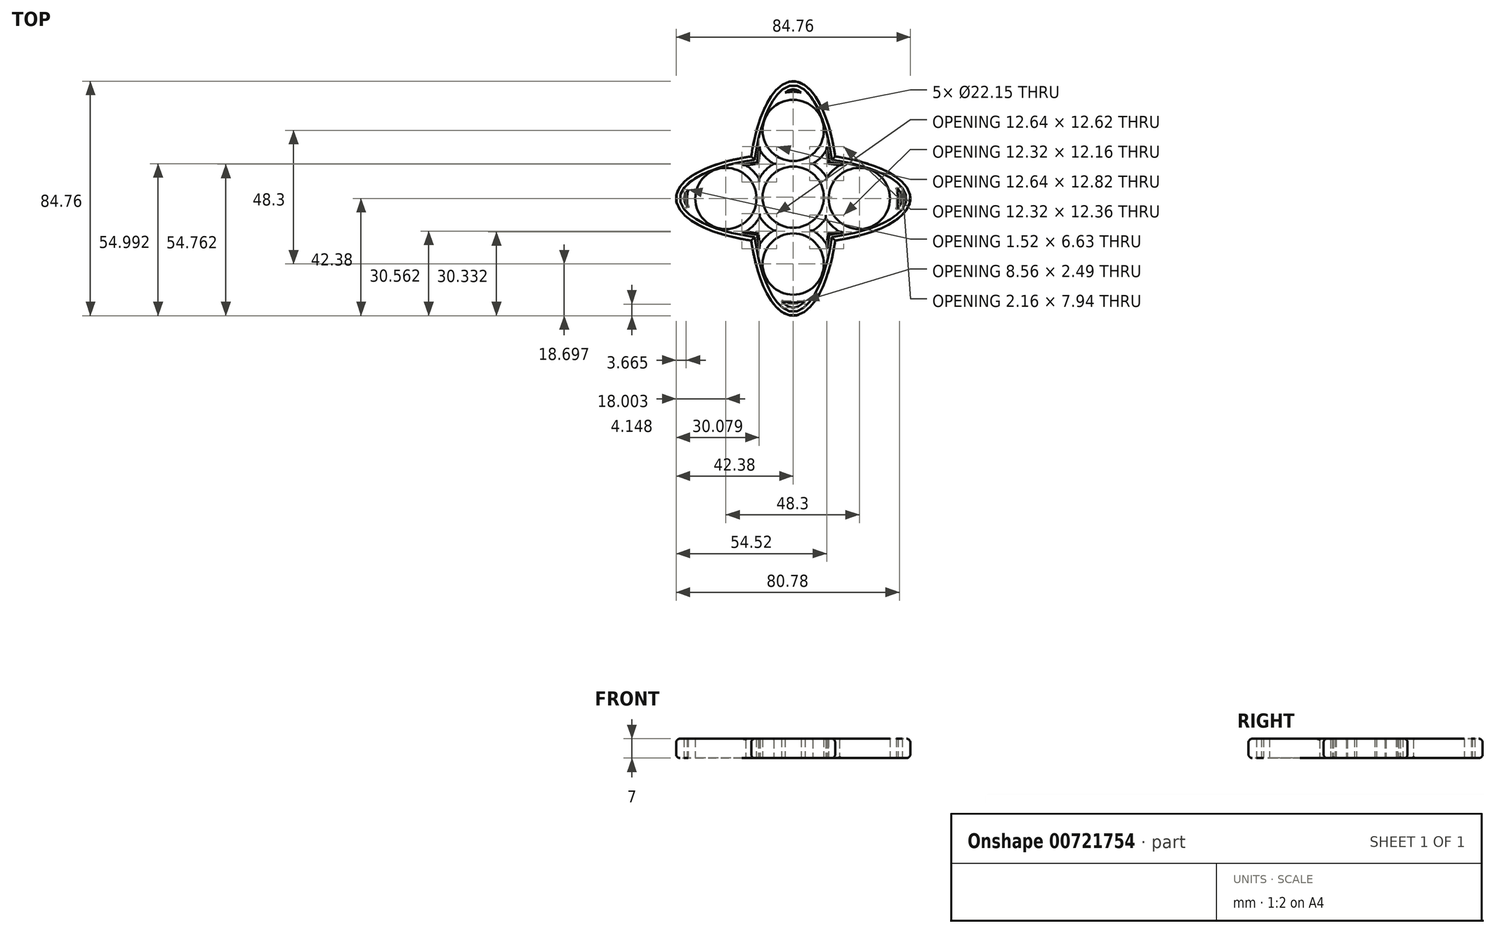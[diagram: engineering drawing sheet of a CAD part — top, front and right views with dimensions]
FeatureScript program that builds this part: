
annotation { "Feature Type Name" : "Feature", "Feature Type Description" : "" }
export const myFeature = defineFeature(function(context is Context, id is Id, definition is map)
    precondition{}
    {
        {
            var Q0;
            Q0=qCreatedBy(makeId("Top.planeOp"),FACE);
            var sketch = newSketch(context, id + "F0", { "sketchPlane" : qUnion([Q0])});
            skCircle(sketch, "E0", {"center": v(0, 0.47) * mm, "radius": 11.07 * mm});
            skCircle(sketch, "E1", {"center": v(0, -23.68) * mm, "radius": 11.07 * mm});
            skCircle(sketch, "E2", {"center": v(0, 24.62) * mm, "radius": 11.07 * mm});
            skCircle(sketch, "E3", {"center": v(23.92, 0) * mm, "radius": 11.07 * mm});
            skCircle(sketch, "E4", {"center": v(-24.38, 0) * mm, "radius": 11.07 * mm});
            skEllipse(sketch, "E5", {"center": v(0, 0) * mm, "majorRadius": 42.38 * mm, "minorRadius": 16.28 * mm, "majorAxis": v(0, -1)});
            skEllipse(sketch, "E6", {"center": v(0, 0) * mm, "majorRadius": 42.38 * mm, "minorRadius": 16.28 * mm, "majorAxis": v(1, 0)});
            skSolve(sketch);
        }
        {
            var Q0;
            {var subQ0=sQuery(id+"F0.wireOp",EDGE,"E6");var subQ1=sQuery(id+"F0.wireOp",EDGE,"E2");var subQ2=makeQuery(id+"F0.imprint","INTERSECT",VERTEX,{"disambiguationData":[OD(0.0)],"derivedFrom":[subQ1,subQ0]});Q0=makeQuery(id+"F0.imprint","IMPRINT",FACE,{"disambiguationData":[TD([[makeQuery(id+"F0.imprint","IMPRINT",EDGE,{"disambiguationData":[TD([[subQ2,-1.0]])],"derivedFrom":subQ1}),-1.0]])]});}
            var Q1;
            Q1=makeQuery(id+"F0.imprint","IMPRINT",FACE,{"disambiguationData":[TD([[makeQuery(id+"F0.imprint","IMPRINT",EDGE,{"derivedFrom":sQuery(id+"F0.wireOp",EDGE,"E0")}),-1.0]])]});
            var Q2;
            {var subQ0=sQuery(id+"F0.wireOp",EDGE,"E5");var subQ1=sQuery(id+"F0.wireOp",EDGE,"E4");var subQ2=makeQuery(id+"F0.imprint","INTERSECT",VERTEX,{"disambiguationData":[OD(0.0)],"derivedFrom":[subQ1,subQ0]});Q2=makeQuery(id+"F0.imprint","IMPRINT",FACE,{"disambiguationData":[TD([[makeQuery(id+"F0.imprint","IMPRINT",EDGE,{"disambiguationData":[TD([[subQ2,-1.0]])],"derivedFrom":subQ1}),-1.0]])]});}
            var Q3;
            {var subQ0=sQuery(id+"F0.wireOp",EDGE,"E6");var subQ1=sQuery(id+"F0.wireOp",EDGE,"E1");var subQ2=makeQuery(id+"F0.imprint","INTERSECT",VERTEX,{"disambiguationData":[OD(0.0)],"derivedFrom":[subQ1,subQ0]});Q3=makeQuery(id+"F0.imprint","IMPRINT",FACE,{"disambiguationData":[TD([[makeQuery(id+"F0.imprint","IMPRINT",EDGE,{"disambiguationData":[TD([[subQ2,-1.0]])],"derivedFrom":subQ1}),-1.0]])]});}
            var Q4;
            {var subQ0=sQuery(id+"F0.wireOp",EDGE,"E5");var subQ1=sQuery(id+"F0.wireOp",EDGE,"E3");var subQ2=makeQuery(id+"F0.imprint","INTERSECT",VERTEX,{"disambiguationData":[OD(0.0)],"derivedFrom":[subQ1,subQ0]});Q4=makeQuery(id+"F0.imprint","IMPRINT",FACE,{"disambiguationData":[TD([[makeQuery(id+"F0.imprint","IMPRINT",EDGE,{"disambiguationData":[TD([[subQ2,-1.0]])],"derivedFrom":subQ1}),-1.0]])]});}
            extrude(context, id + "F1", {"entities" : qUnion([Q0, Q1, Q2, Q3, Q4]), "depth" : 7 * mm, "offsetDistance" : 25 * mm});
        }
        {
            var Q0;
            {var subQ0=sQuery(id+"F0.wireOp",EDGE,"E6");var subQ1=sQuery(id+"F0.wireOp",EDGE,"E5");Q0=makeQuery(id+"F1.opExtrude","CAP_EDGE",EDGE,{"disambiguationData":[OSD([subQ1]),TDD([makeQuery(id+"F0.imprint","IMPRINT",EDGE,{"disambiguationData":[TD([[makeQuery(id+"F0.imprint","INTERSECT",VERTEX,{"disambiguationData":[OD(1.0)],"derivedFrom":[subQ1,subQ0]}),-1.0]])],"derivedFrom":subQ1})])],"isStart":false});}
            var Q1;
            {var subQ0=sQuery(id+"F0.wireOp",EDGE,"E6");var subQ1=sQuery(id+"F0.wireOp",EDGE,"E5");Q1=makeQuery(id+"F1.opExtrude","CAP_EDGE",EDGE,{"disambiguationData":[OSD([subQ0]),TDD([makeQuery(id+"F0.imprint","IMPRINT",EDGE,{"disambiguationData":[TD([[makeQuery(id+"F0.imprint","INTERSECT",VERTEX,{"disambiguationData":[OD(0.0)],"derivedFrom":[subQ1,subQ0]}),-1.0]])],"derivedFrom":subQ0})])],"isStart":false});}
            var Q2;
            {var subQ0=sQuery(id+"F0.wireOp",EDGE,"E6");var subQ1=sQuery(id+"F0.wireOp",EDGE,"E5");Q2=makeQuery(id+"F1.opExtrude","CAP_EDGE",EDGE,{"disambiguationData":[OSD([subQ1]),TDD([makeQuery(id+"F0.imprint","IMPRINT",EDGE,{"disambiguationData":[TD([[makeQuery(id+"F0.imprint","INTERSECT",VERTEX,{"disambiguationData":[OD(0.0)],"derivedFrom":[subQ1,subQ0]}),1.0]])],"derivedFrom":subQ1})])],"isStart":false});}
            var Q3;
            {var subQ0=sQuery(id+"F0.wireOp",EDGE,"E6");var subQ1=sQuery(id+"F0.wireOp",EDGE,"E5");Q3=makeQuery(id+"F1.opExtrude","CAP_EDGE",EDGE,{"disambiguationData":[OSD([subQ0]),TDD([makeQuery(id+"F0.imprint","IMPRINT",EDGE,{"disambiguationData":[TD([[makeQuery(id+"F0.imprint","INTERSECT",VERTEX,{"disambiguationData":[OD(2.0)],"derivedFrom":[subQ1,subQ0]}),-1.0]])],"derivedFrom":subQ0})])],"isStart":false});}
            var Q4;
            {var subQ0=sQuery(id+"F0.wireOp",EDGE,"E6");var subQ1=sQuery(id+"F0.wireOp",EDGE,"E5");Q4=makeQuery(id+"F1.opExtrude","CAP_EDGE",EDGE,{"disambiguationData":[OSD([subQ0]),TDD([makeQuery(id+"F0.imprint","IMPRINT",EDGE,{"disambiguationData":[TD([[makeQuery(id+"F0.imprint","INTERSECT",VERTEX,{"disambiguationData":[OD(0.0)],"derivedFrom":[subQ1,subQ0]}),-1.0]])],"derivedFrom":subQ0})])],"isStart":true});}
            var Q5;
            {var subQ0=sQuery(id+"F0.wireOp",EDGE,"E6");var subQ1=sQuery(id+"F0.wireOp",EDGE,"E5");Q5=makeQuery(id+"F1.opExtrude","CAP_EDGE",EDGE,{"disambiguationData":[OSD([subQ1]),TDD([makeQuery(id+"F0.imprint","IMPRINT",EDGE,{"disambiguationData":[TD([[makeQuery(id+"F0.imprint","INTERSECT",VERTEX,{"disambiguationData":[OD(0.0)],"derivedFrom":[subQ1,subQ0]}),1.0]])],"derivedFrom":subQ1})])],"isStart":true});}
            var Q6;
            {var subQ0=sQuery(id+"F0.wireOp",EDGE,"E6");var subQ1=sQuery(id+"F0.wireOp",EDGE,"E5");Q6=makeQuery(id+"F1.opExtrude","CAP_EDGE",EDGE,{"disambiguationData":[OSD([subQ0]),TDD([makeQuery(id+"F0.imprint","IMPRINT",EDGE,{"disambiguationData":[TD([[makeQuery(id+"F0.imprint","INTERSECT",VERTEX,{"disambiguationData":[OD(2.0)],"derivedFrom":[subQ1,subQ0]}),-1.0]])],"derivedFrom":subQ0})])],"isStart":true});}
            var Q7;
            {var subQ0=sQuery(id+"F0.wireOp",EDGE,"E6");var subQ1=sQuery(id+"F0.wireOp",EDGE,"E5");Q7=makeQuery(id+"F1.opExtrude","CAP_EDGE",EDGE,{"disambiguationData":[OSD([subQ1]),TDD([makeQuery(id+"F0.imprint","IMPRINT",EDGE,{"disambiguationData":[TD([[makeQuery(id+"F0.imprint","INTERSECT",VERTEX,{"disambiguationData":[OD(1.0)],"derivedFrom":[subQ1,subQ0]}),-1.0]])],"derivedFrom":subQ1})])],"isStart":true});}
            fillet(context, id + "F2", {"entities" : qUnion([Q0, Q1, Q2, Q3, Q4, Q5, Q6, Q7]), "radius" : 1.4 * mm, "tangentPropagation" : true, "allowEdgeOverflow" : false});
        }
        {
            var Q0;
            Q0=makeQuery(id+"F1.opExtrude","CAP_FACE",FACE,{"disambiguationData":[OSD([sQuery(id+"F0.wireOp",EDGE,"E0"),sQuery(id+"F0.wireOp",EDGE,"E1"),sQuery(id+"F0.wireOp",EDGE,"E2"),sQuery(id+"F0.wireOp",EDGE,"E3"),sQuery(id+"F0.wireOp",EDGE,"E4"),sQuery(id+"F0.wireOp",EDGE,"E5"),sQuery(id+"F0.wireOp",EDGE,"E6")])],"isStart":false});
            var Q1;
            Q1=makeQuery(id+"F1.opExtrude","CAP_FACE",FACE,{"disambiguationData":[OSD([sQuery(id+"F0.wireOp",EDGE,"E0"),sQuery(id+"F0.wireOp",EDGE,"E1"),sQuery(id+"F0.wireOp",EDGE,"E2"),sQuery(id+"F0.wireOp",EDGE,"E3"),sQuery(id+"F0.wireOp",EDGE,"E4"),sQuery(id+"F0.wireOp",EDGE,"E5"),sQuery(id+"F0.wireOp",EDGE,"E6")])],"isStart":true});
            shell(context, id + "F3", {"entities" : qUnion([Q0, Q1]), "thickness" : 2.9 * mm});
        }
        {
            var Q0;
            {var subQ0=sQuery(id+"F0.wireOp",EDGE,"E6");var subQ1=sQuery(id+"F0.wireOp",EDGE,"E5");var subQ2=makeQuery(id+"F0.imprint","IMPRINT",EDGE,{"disambiguationData":[TD([[makeQuery(id+"F0.imprint","INTERSECT",VERTEX,{"disambiguationData":[OD(1.0)],"derivedFrom":[subQ1,subQ0]}),-1.0]])],"derivedFrom":subQ1});var subQ3=makeQuery(id+"F1.opExtrude","CAP_EDGE",EDGE,{"disambiguationData":[OSD([subQ1]),TDD([subQ2])],"isStart":false});var subQ4=sQuery(id+"F0.wireOp",EDGE,"E4");var subQ5=sQuery(id+"F0.wireOp",EDGE,"E3");var subQ6=sQuery(id+"F0.wireOp",EDGE,"E2");var subQ7=sQuery(id+"F0.wireOp",EDGE,"E1");var subQ8=sQuery(id+"F0.wireOp",EDGE,"E0");Q0=makeQuery(id+"F3.opShell","OFFSET_EDGE",EDGE,{"disambiguationData":[OSD([subQ8,subQ7,subQ6,subQ5,subQ4,subQ1,subQ0]),TDD([makeQuery(id+"F2.opFillet","BLEND_EDGE",EDGE,{"blendedFrom":[subQ3,makeQuery(id+"F1.opExtrude","CAP_FACE",FACE,{"disambiguationData":[OSD([subQ8,subQ7,subQ6,subQ5,subQ4,subQ1,subQ0])],"isStart":false})],"blendedInto":[makeQuery(id+"F1.opExtrude","CAP_FACE",FACE,{"disambiguationData":[OSD([subQ8,subQ7,subQ6,subQ5,subQ4,subQ1,subQ0])],"isStart":false})]}),makeQuery(id+"F2.opFillet","BLEND_EDGE",EDGE,{"blendedFrom":[subQ3,makeQuery(id+"F1.opExtrude","SWEPT_FACE",FACE,{"disambiguationData":[OSD([subQ1]),TDD([subQ2])]})],"blendedInto":[makeQuery(id+"F1.opExtrude","SWEPT_FACE",FACE,{"disambiguationData":[OSD([subQ1]),TDD([subQ2])]})]})]),OD(1.0)]});}
            var Q1;
            {var subQ0=sQuery(id+"F0.wireOp",EDGE,"E6");var subQ1=sQuery(id+"F0.wireOp",EDGE,"E5");var subQ2=makeQuery(id+"F0.imprint","IMPRINT",EDGE,{"disambiguationData":[TD([[makeQuery(id+"F0.imprint","INTERSECT",VERTEX,{"disambiguationData":[OD(0.0)],"derivedFrom":[subQ1,subQ0]}),-1.0]])],"derivedFrom":subQ0});var subQ3=makeQuery(id+"F1.opExtrude","CAP_EDGE",EDGE,{"disambiguationData":[OSD([subQ0]),TDD([subQ2])],"isStart":false});var subQ4=sQuery(id+"F0.wireOp",EDGE,"E4");var subQ5=sQuery(id+"F0.wireOp",EDGE,"E3");var subQ6=sQuery(id+"F0.wireOp",EDGE,"E2");var subQ7=sQuery(id+"F0.wireOp",EDGE,"E1");var subQ8=sQuery(id+"F0.wireOp",EDGE,"E0");Q1=makeQuery(id+"F3.opShell","OFFSET_EDGE",EDGE,{"disambiguationData":[OSD([subQ8,subQ7,subQ6,subQ5,subQ4,subQ1,subQ0]),TDD([makeQuery(id+"F2.opFillet","BLEND_EDGE",EDGE,{"blendedFrom":[subQ3,makeQuery(id+"F1.opExtrude","CAP_FACE",FACE,{"disambiguationData":[OSD([subQ8,subQ7,subQ6,subQ5,subQ4,subQ1,subQ0])],"isStart":false})],"blendedInto":[makeQuery(id+"F1.opExtrude","CAP_FACE",FACE,{"disambiguationData":[OSD([subQ8,subQ7,subQ6,subQ5,subQ4,subQ1,subQ0])],"isStart":false})]}),makeQuery(id+"F2.opFillet","BLEND_EDGE",EDGE,{"blendedFrom":[subQ3,makeQuery(id+"F1.opExtrude","SWEPT_FACE",FACE,{"disambiguationData":[OSD([subQ0]),TDD([subQ2])]})],"blendedInto":[makeQuery(id+"F1.opExtrude","SWEPT_FACE",FACE,{"disambiguationData":[OSD([subQ0]),TDD([subQ2])]})]})]),OD(0.0)]});}
            var Q2;
            {var subQ0=sQuery(id+"F0.wireOp",EDGE,"E3");Q2=makeQuery(id+"F3.opShell","OFFSET_EDGE",EDGE,{"disambiguationData":[OSD([subQ0]),TDD([makeQuery(id+"F1.opExtrude","CAP_EDGE",EDGE,{"disambiguationData":[OSD([subQ0])],"isStart":false})]),OD(1.0)]});}
            var Q3;
            {var subQ0=sQuery(id+"F0.wireOp",EDGE,"E0");Q3=makeQuery(id+"F3.opShell","OFFSET_EDGE",EDGE,{"disambiguationData":[OSD([subQ0]),TDD([makeQuery(id+"F1.opExtrude","CAP_EDGE",EDGE,{"disambiguationData":[OSD([subQ0])],"isStart":false})]),OD(2.0)]});}
            var Q4;
            {var subQ0=sQuery(id+"F0.wireOp",EDGE,"E2");Q4=makeQuery(id+"F3.opShell","OFFSET_EDGE",EDGE,{"disambiguationData":[OSD([subQ0]),TDD([makeQuery(id+"F1.opExtrude","CAP_EDGE",EDGE,{"disambiguationData":[OSD([subQ0])],"isStart":false})]),OD(2.0)]});}
            var Q5;
            {var subQ0=sQuery(id+"F0.wireOp",EDGE,"E2");Q5=makeQuery(id+"F3.opShell","OFFSET_EDGE",EDGE,{"disambiguationData":[OSD([subQ0]),TDD([makeQuery(id+"F1.opExtrude","CAP_EDGE",EDGE,{"disambiguationData":[OSD([subQ0])],"isStart":false})]),OD(1.0)]});}
            var Q6;
            {var subQ0=sQuery(id+"F0.wireOp",EDGE,"E6");var subQ1=sQuery(id+"F0.wireOp",EDGE,"E5");var subQ2=makeQuery(id+"F0.imprint","IMPRINT",EDGE,{"disambiguationData":[TD([[makeQuery(id+"F0.imprint","INTERSECT",VERTEX,{"disambiguationData":[OD(1.0)],"derivedFrom":[subQ1,subQ0]}),-1.0]])],"derivedFrom":subQ1});var subQ3=makeQuery(id+"F1.opExtrude","CAP_EDGE",EDGE,{"disambiguationData":[OSD([subQ1]),TDD([subQ2])],"isStart":false});var subQ4=sQuery(id+"F0.wireOp",EDGE,"E4");var subQ5=sQuery(id+"F0.wireOp",EDGE,"E3");var subQ6=sQuery(id+"F0.wireOp",EDGE,"E2");var subQ7=sQuery(id+"F0.wireOp",EDGE,"E1");var subQ8=sQuery(id+"F0.wireOp",EDGE,"E0");Q6=makeQuery(id+"F3.opShell","OFFSET_EDGE",EDGE,{"disambiguationData":[OSD([subQ8,subQ7,subQ6,subQ5,subQ4,subQ1,subQ0]),TDD([makeQuery(id+"F2.opFillet","BLEND_EDGE",EDGE,{"blendedFrom":[subQ3,makeQuery(id+"F1.opExtrude","CAP_FACE",FACE,{"disambiguationData":[OSD([subQ8,subQ7,subQ6,subQ5,subQ4,subQ1,subQ0])],"isStart":false})],"blendedInto":[makeQuery(id+"F1.opExtrude","CAP_FACE",FACE,{"disambiguationData":[OSD([subQ8,subQ7,subQ6,subQ5,subQ4,subQ1,subQ0])],"isStart":false})]}),makeQuery(id+"F2.opFillet","BLEND_EDGE",EDGE,{"blendedFrom":[subQ3,makeQuery(id+"F1.opExtrude","SWEPT_FACE",FACE,{"disambiguationData":[OSD([subQ1]),TDD([subQ2])]})],"blendedInto":[makeQuery(id+"F1.opExtrude","SWEPT_FACE",FACE,{"disambiguationData":[OSD([subQ1]),TDD([subQ2])]})]})]),OD(0.0)]});}
            var Q7;
            {var subQ0=sQuery(id+"F0.wireOp",EDGE,"E6");var subQ1=sQuery(id+"F0.wireOp",EDGE,"E5");var subQ2=makeQuery(id+"F0.imprint","IMPRINT",EDGE,{"disambiguationData":[TD([[makeQuery(id+"F0.imprint","INTERSECT",VERTEX,{"disambiguationData":[OD(2.0)],"derivedFrom":[subQ1,subQ0]}),-1.0]])],"derivedFrom":subQ0});var subQ3=makeQuery(id+"F1.opExtrude","CAP_EDGE",EDGE,{"disambiguationData":[OSD([subQ0]),TDD([subQ2])],"isStart":false});var subQ4=sQuery(id+"F0.wireOp",EDGE,"E4");var subQ5=sQuery(id+"F0.wireOp",EDGE,"E3");var subQ6=sQuery(id+"F0.wireOp",EDGE,"E2");var subQ7=sQuery(id+"F0.wireOp",EDGE,"E1");var subQ8=sQuery(id+"F0.wireOp",EDGE,"E0");Q7=makeQuery(id+"F3.opShell","OFFSET_EDGE",EDGE,{"disambiguationData":[OSD([subQ8,subQ7,subQ6,subQ5,subQ4,subQ1,subQ0]),TDD([makeQuery(id+"F2.opFillet","BLEND_EDGE",EDGE,{"blendedFrom":[subQ3,makeQuery(id+"F1.opExtrude","CAP_FACE",FACE,{"disambiguationData":[OSD([subQ8,subQ7,subQ6,subQ5,subQ4,subQ1,subQ0])],"isStart":false})],"blendedInto":[makeQuery(id+"F1.opExtrude","CAP_FACE",FACE,{"disambiguationData":[OSD([subQ8,subQ7,subQ6,subQ5,subQ4,subQ1,subQ0])],"isStart":false})]}),makeQuery(id+"F2.opFillet","BLEND_EDGE",EDGE,{"blendedFrom":[subQ3,makeQuery(id+"F1.opExtrude","SWEPT_FACE",FACE,{"disambiguationData":[OSD([subQ0]),TDD([subQ2])]})],"blendedInto":[makeQuery(id+"F1.opExtrude","SWEPT_FACE",FACE,{"disambiguationData":[OSD([subQ0]),TDD([subQ2])]})]})]),OD(0.0)]});}
            var Q8;
            {var subQ0=sQuery(id+"F0.wireOp",EDGE,"E4");Q8=makeQuery(id+"F3.opShell","OFFSET_EDGE",EDGE,{"disambiguationData":[OSD([subQ0]),TDD([makeQuery(id+"F1.opExtrude","CAP_EDGE",EDGE,{"disambiguationData":[OSD([subQ0])],"isStart":false})]),OD(1.0)]});}
            var Q9;
            {var subQ0=sQuery(id+"F0.wireOp",EDGE,"E0");Q9=makeQuery(id+"F3.opShell","OFFSET_EDGE",EDGE,{"disambiguationData":[OSD([subQ0]),TDD([makeQuery(id+"F1.opExtrude","CAP_EDGE",EDGE,{"disambiguationData":[OSD([subQ0])],"isStart":false})]),OD(3.0)]});}
            var Q10;
            {var subQ0=sQuery(id+"F0.wireOp",EDGE,"E0");Q10=makeQuery(id+"F3.opShell","OFFSET_EDGE",EDGE,{"disambiguationData":[OSD([subQ0]),TDD([makeQuery(id+"F1.opExtrude","CAP_EDGE",EDGE,{"disambiguationData":[OSD([subQ0])],"isStart":false})]),OD(0.0)]});}
            var Q11;
            {var subQ0=sQuery(id+"F0.wireOp",EDGE,"E3");Q11=makeQuery(id+"F3.opShell","OFFSET_EDGE",EDGE,{"disambiguationData":[OSD([subQ0]),TDD([makeQuery(id+"F1.opExtrude","CAP_EDGE",EDGE,{"disambiguationData":[OSD([subQ0])],"isStart":false})]),OD(2.0)]});}
            var Q12;
            {var subQ0=sQuery(id+"F0.wireOp",EDGE,"E6");var subQ1=sQuery(id+"F0.wireOp",EDGE,"E5");var subQ2=makeQuery(id+"F0.imprint","IMPRINT",EDGE,{"disambiguationData":[TD([[makeQuery(id+"F0.imprint","INTERSECT",VERTEX,{"disambiguationData":[OD(0.0)],"derivedFrom":[subQ1,subQ0]}),-1.0]])],"derivedFrom":subQ0});var subQ3=makeQuery(id+"F1.opExtrude","CAP_EDGE",EDGE,{"disambiguationData":[OSD([subQ0]),TDD([subQ2])],"isStart":false});var subQ4=sQuery(id+"F0.wireOp",EDGE,"E4");var subQ5=sQuery(id+"F0.wireOp",EDGE,"E3");var subQ6=sQuery(id+"F0.wireOp",EDGE,"E2");var subQ7=sQuery(id+"F0.wireOp",EDGE,"E1");var subQ8=sQuery(id+"F0.wireOp",EDGE,"E0");Q12=makeQuery(id+"F3.opShell","OFFSET_EDGE",EDGE,{"disambiguationData":[OSD([subQ8,subQ7,subQ6,subQ5,subQ4,subQ1,subQ0]),TDD([makeQuery(id+"F2.opFillet","BLEND_EDGE",EDGE,{"blendedFrom":[subQ3,makeQuery(id+"F1.opExtrude","CAP_FACE",FACE,{"disambiguationData":[OSD([subQ8,subQ7,subQ6,subQ5,subQ4,subQ1,subQ0])],"isStart":false})],"blendedInto":[makeQuery(id+"F1.opExtrude","CAP_FACE",FACE,{"disambiguationData":[OSD([subQ8,subQ7,subQ6,subQ5,subQ4,subQ1,subQ0])],"isStart":false})]}),makeQuery(id+"F2.opFillet","BLEND_EDGE",EDGE,{"blendedFrom":[subQ3,makeQuery(id+"F1.opExtrude","SWEPT_FACE",FACE,{"disambiguationData":[OSD([subQ0]),TDD([subQ2])]})],"blendedInto":[makeQuery(id+"F1.opExtrude","SWEPT_FACE",FACE,{"disambiguationData":[OSD([subQ0]),TDD([subQ2])]})]})]),OD(1.0)]});}
            var Q13;
            {var subQ0=sQuery(id+"F0.wireOp",EDGE,"E1");Q13=makeQuery(id+"F3.opShell","OFFSET_EDGE",EDGE,{"disambiguationData":[OSD([subQ0]),TDD([makeQuery(id+"F1.opExtrude","CAP_EDGE",EDGE,{"disambiguationData":[OSD([subQ0])],"isStart":false})]),OD(2.0)]});}
            var Q14;
            {var subQ0=sQuery(id+"F0.wireOp",EDGE,"E0");Q14=makeQuery(id+"F3.opShell","OFFSET_EDGE",EDGE,{"disambiguationData":[OSD([subQ0]),TDD([makeQuery(id+"F1.opExtrude","CAP_EDGE",EDGE,{"disambiguationData":[OSD([subQ0])],"isStart":false})]),OD(1.0)]});}
            var Q15;
            {var subQ0=sQuery(id+"F0.wireOp",EDGE,"E4");Q15=makeQuery(id+"F3.opShell","OFFSET_EDGE",EDGE,{"disambiguationData":[OSD([subQ0]),TDD([makeQuery(id+"F1.opExtrude","CAP_EDGE",EDGE,{"disambiguationData":[OSD([subQ0])],"isStart":false})]),OD(2.0)]});}
            var Q16;
            {var subQ0=sQuery(id+"F0.wireOp",EDGE,"E6");var subQ1=sQuery(id+"F0.wireOp",EDGE,"E5");var subQ2=makeQuery(id+"F0.imprint","IMPRINT",EDGE,{"disambiguationData":[TD([[makeQuery(id+"F0.imprint","INTERSECT",VERTEX,{"disambiguationData":[OD(2.0)],"derivedFrom":[subQ1,subQ0]}),-1.0]])],"derivedFrom":subQ0});var subQ3=makeQuery(id+"F1.opExtrude","CAP_EDGE",EDGE,{"disambiguationData":[OSD([subQ0]),TDD([subQ2])],"isStart":false});var subQ4=sQuery(id+"F0.wireOp",EDGE,"E4");var subQ5=sQuery(id+"F0.wireOp",EDGE,"E3");var subQ6=sQuery(id+"F0.wireOp",EDGE,"E2");var subQ7=sQuery(id+"F0.wireOp",EDGE,"E1");var subQ8=sQuery(id+"F0.wireOp",EDGE,"E0");Q16=makeQuery(id+"F3.opShell","OFFSET_EDGE",EDGE,{"disambiguationData":[OSD([subQ8,subQ7,subQ6,subQ5,subQ4,subQ1,subQ0]),TDD([makeQuery(id+"F2.opFillet","BLEND_EDGE",EDGE,{"blendedFrom":[subQ3,makeQuery(id+"F1.opExtrude","CAP_FACE",FACE,{"disambiguationData":[OSD([subQ8,subQ7,subQ6,subQ5,subQ4,subQ1,subQ0])],"isStart":false})],"blendedInto":[makeQuery(id+"F1.opExtrude","CAP_FACE",FACE,{"disambiguationData":[OSD([subQ8,subQ7,subQ6,subQ5,subQ4,subQ1,subQ0])],"isStart":false})]}),makeQuery(id+"F2.opFillet","BLEND_EDGE",EDGE,{"blendedFrom":[subQ3,makeQuery(id+"F1.opExtrude","SWEPT_FACE",FACE,{"disambiguationData":[OSD([subQ0]),TDD([subQ2])]})],"blendedInto":[makeQuery(id+"F1.opExtrude","SWEPT_FACE",FACE,{"disambiguationData":[OSD([subQ0]),TDD([subQ2])]})]})]),OD(1.0)]});}
            var Q17;
            {var subQ0=sQuery(id+"F0.wireOp",EDGE,"E6");var subQ1=sQuery(id+"F0.wireOp",EDGE,"E5");var subQ2=makeQuery(id+"F0.imprint","IMPRINT",EDGE,{"disambiguationData":[TD([[makeQuery(id+"F0.imprint","INTERSECT",VERTEX,{"disambiguationData":[OD(0.0)],"derivedFrom":[subQ1,subQ0]}),1.0]])],"derivedFrom":subQ1});var subQ3=makeQuery(id+"F1.opExtrude","CAP_EDGE",EDGE,{"disambiguationData":[OSD([subQ1]),TDD([subQ2])],"isStart":false});var subQ4=sQuery(id+"F0.wireOp",EDGE,"E4");var subQ5=sQuery(id+"F0.wireOp",EDGE,"E3");var subQ6=sQuery(id+"F0.wireOp",EDGE,"E2");var subQ7=sQuery(id+"F0.wireOp",EDGE,"E1");var subQ8=sQuery(id+"F0.wireOp",EDGE,"E0");Q17=makeQuery(id+"F3.opShell","OFFSET_EDGE",EDGE,{"disambiguationData":[OSD([subQ8,subQ7,subQ6,subQ5,subQ4,subQ1,subQ0]),TDD([makeQuery(id+"F2.opFillet","BLEND_EDGE",EDGE,{"blendedFrom":[subQ3,makeQuery(id+"F1.opExtrude","CAP_FACE",FACE,{"disambiguationData":[OSD([subQ8,subQ7,subQ6,subQ5,subQ4,subQ1,subQ0])],"isStart":false})],"blendedInto":[makeQuery(id+"F1.opExtrude","CAP_FACE",FACE,{"disambiguationData":[OSD([subQ8,subQ7,subQ6,subQ5,subQ4,subQ1,subQ0])],"isStart":false})]}),makeQuery(id+"F2.opFillet","BLEND_EDGE",EDGE,{"blendedFrom":[subQ3,makeQuery(id+"F1.opExtrude","SWEPT_FACE",FACE,{"disambiguationData":[OSD([subQ1]),TDD([subQ2])]})],"blendedInto":[makeQuery(id+"F1.opExtrude","SWEPT_FACE",FACE,{"disambiguationData":[OSD([subQ1]),TDD([subQ2])]})]})]),OD(0.0)]});}
            var Q18;
            {var subQ0=sQuery(id+"F0.wireOp",EDGE,"E1");Q18=makeQuery(id+"F3.opShell","OFFSET_EDGE",EDGE,{"disambiguationData":[OSD([subQ0]),TDD([makeQuery(id+"F1.opExtrude","CAP_EDGE",EDGE,{"disambiguationData":[OSD([subQ0])],"isStart":false})]),OD(1.0)]});}
            var Q19;
            {var subQ0=sQuery(id+"F0.wireOp",EDGE,"E6");var subQ1=sQuery(id+"F0.wireOp",EDGE,"E5");var subQ2=makeQuery(id+"F0.imprint","IMPRINT",EDGE,{"disambiguationData":[TD([[makeQuery(id+"F0.imprint","INTERSECT",VERTEX,{"disambiguationData":[OD(0.0)],"derivedFrom":[subQ1,subQ0]}),1.0]])],"derivedFrom":subQ1});var subQ3=makeQuery(id+"F1.opExtrude","CAP_EDGE",EDGE,{"disambiguationData":[OSD([subQ1]),TDD([subQ2])],"isStart":false});var subQ4=sQuery(id+"F0.wireOp",EDGE,"E4");var subQ5=sQuery(id+"F0.wireOp",EDGE,"E3");var subQ6=sQuery(id+"F0.wireOp",EDGE,"E2");var subQ7=sQuery(id+"F0.wireOp",EDGE,"E1");var subQ8=sQuery(id+"F0.wireOp",EDGE,"E0");Q19=makeQuery(id+"F3.opShell","OFFSET_EDGE",EDGE,{"disambiguationData":[OSD([subQ8,subQ7,subQ6,subQ5,subQ4,subQ1,subQ0]),TDD([makeQuery(id+"F2.opFillet","BLEND_EDGE",EDGE,{"blendedFrom":[subQ3,makeQuery(id+"F1.opExtrude","CAP_FACE",FACE,{"disambiguationData":[OSD([subQ8,subQ7,subQ6,subQ5,subQ4,subQ1,subQ0])],"isStart":false})],"blendedInto":[makeQuery(id+"F1.opExtrude","CAP_FACE",FACE,{"disambiguationData":[OSD([subQ8,subQ7,subQ6,subQ5,subQ4,subQ1,subQ0])],"isStart":false})]}),makeQuery(id+"F2.opFillet","BLEND_EDGE",EDGE,{"blendedFrom":[subQ3,makeQuery(id+"F1.opExtrude","SWEPT_FACE",FACE,{"disambiguationData":[OSD([subQ1]),TDD([subQ2])]})],"blendedInto":[makeQuery(id+"F1.opExtrude","SWEPT_FACE",FACE,{"disambiguationData":[OSD([subQ1]),TDD([subQ2])]})]})]),OD(1.0)]});}
            var Q20;
            {var subQ0=sQuery(id+"F0.wireOp",EDGE,"E1");Q20=makeQuery(id+"F3.opShell","OFFSET_EDGE",EDGE,{"disambiguationData":[OSD([subQ0]),TDD([makeQuery(id+"F1.opExtrude","CAP_EDGE",EDGE,{"disambiguationData":[OSD([subQ0])],"isStart":true})]),OD(2.0)]});}
            var Q21;
            {var subQ0=sQuery(id+"F0.wireOp",EDGE,"E6");var subQ1=sQuery(id+"F0.wireOp",EDGE,"E5");var subQ2=makeQuery(id+"F0.imprint","IMPRINT",EDGE,{"disambiguationData":[TD([[makeQuery(id+"F0.imprint","INTERSECT",VERTEX,{"disambiguationData":[OD(0.0)],"derivedFrom":[subQ1,subQ0]}),1.0]])],"derivedFrom":subQ1});var subQ3=makeQuery(id+"F1.opExtrude","CAP_EDGE",EDGE,{"disambiguationData":[OSD([subQ1]),TDD([subQ2])],"isStart":true});var subQ4=sQuery(id+"F0.wireOp",EDGE,"E4");var subQ5=sQuery(id+"F0.wireOp",EDGE,"E3");var subQ6=sQuery(id+"F0.wireOp",EDGE,"E2");var subQ7=sQuery(id+"F0.wireOp",EDGE,"E1");var subQ8=sQuery(id+"F0.wireOp",EDGE,"E0");Q21=makeQuery(id+"F3.opShell","OFFSET_EDGE",EDGE,{"disambiguationData":[OSD([subQ8,subQ7,subQ6,subQ5,subQ4,subQ1,subQ0]),TDD([makeQuery(id+"F2.opFillet","BLEND_EDGE",EDGE,{"blendedFrom":[subQ3,makeQuery(id+"F1.opExtrude","CAP_FACE",FACE,{"disambiguationData":[OSD([subQ8,subQ7,subQ6,subQ5,subQ4,subQ1,subQ0])],"isStart":true})],"blendedInto":[makeQuery(id+"F1.opExtrude","CAP_FACE",FACE,{"disambiguationData":[OSD([subQ8,subQ7,subQ6,subQ5,subQ4,subQ1,subQ0])],"isStart":true})]}),makeQuery(id+"F2.opFillet","BLEND_EDGE",EDGE,{"blendedFrom":[subQ3,makeQuery(id+"F1.opExtrude","SWEPT_FACE",FACE,{"disambiguationData":[OSD([subQ1]),TDD([subQ2])]})],"blendedInto":[makeQuery(id+"F1.opExtrude","SWEPT_FACE",FACE,{"disambiguationData":[OSD([subQ1]),TDD([subQ2])]})]})]),OD(1.0)]});}
            var Q22;
            {var subQ0=sQuery(id+"F0.wireOp",EDGE,"E0");Q22=makeQuery(id+"F3.opShell","OFFSET_EDGE",EDGE,{"disambiguationData":[OSD([subQ0]),TDD([makeQuery(id+"F1.opExtrude","CAP_EDGE",EDGE,{"disambiguationData":[OSD([subQ0])],"isStart":true})]),OD(0.0)]});}
            var Q23;
            {var subQ0=sQuery(id+"F0.wireOp",EDGE,"E3");Q23=makeQuery(id+"F3.opShell","OFFSET_EDGE",EDGE,{"disambiguationData":[OSD([subQ0]),TDD([makeQuery(id+"F1.opExtrude","CAP_EDGE",EDGE,{"disambiguationData":[OSD([subQ0])],"isStart":true})]),OD(2.0)]});}
            var Q24;
            {var subQ0=sQuery(id+"F0.wireOp",EDGE,"E6");var subQ1=sQuery(id+"F0.wireOp",EDGE,"E5");var subQ2=makeQuery(id+"F0.imprint","IMPRINT",EDGE,{"disambiguationData":[TD([[makeQuery(id+"F0.imprint","INTERSECT",VERTEX,{"disambiguationData":[OD(0.0)],"derivedFrom":[subQ1,subQ0]}),-1.0]])],"derivedFrom":subQ0});var subQ3=makeQuery(id+"F1.opExtrude","CAP_EDGE",EDGE,{"disambiguationData":[OSD([subQ0]),TDD([subQ2])],"isStart":true});var subQ4=sQuery(id+"F0.wireOp",EDGE,"E4");var subQ5=sQuery(id+"F0.wireOp",EDGE,"E3");var subQ6=sQuery(id+"F0.wireOp",EDGE,"E2");var subQ7=sQuery(id+"F0.wireOp",EDGE,"E1");var subQ8=sQuery(id+"F0.wireOp",EDGE,"E0");Q24=makeQuery(id+"F3.opShell","OFFSET_EDGE",EDGE,{"disambiguationData":[OSD([subQ8,subQ7,subQ6,subQ5,subQ4,subQ1,subQ0]),TDD([makeQuery(id+"F2.opFillet","BLEND_EDGE",EDGE,{"blendedFrom":[subQ3,makeQuery(id+"F1.opExtrude","CAP_FACE",FACE,{"disambiguationData":[OSD([subQ8,subQ7,subQ6,subQ5,subQ4,subQ1,subQ0])],"isStart":true})],"blendedInto":[makeQuery(id+"F1.opExtrude","CAP_FACE",FACE,{"disambiguationData":[OSD([subQ8,subQ7,subQ6,subQ5,subQ4,subQ1,subQ0])],"isStart":true})]}),makeQuery(id+"F2.opFillet","BLEND_EDGE",EDGE,{"blendedFrom":[subQ3,makeQuery(id+"F1.opExtrude","SWEPT_FACE",FACE,{"disambiguationData":[OSD([subQ0]),TDD([subQ2])]})],"blendedInto":[makeQuery(id+"F1.opExtrude","SWEPT_FACE",FACE,{"disambiguationData":[OSD([subQ0]),TDD([subQ2])]})]})]),OD(1.0)]});}
            var Q25;
            {var subQ0=sQuery(id+"F0.wireOp",EDGE,"E6");var subQ1=sQuery(id+"F0.wireOp",EDGE,"E5");var subQ2=makeQuery(id+"F0.imprint","IMPRINT",EDGE,{"disambiguationData":[TD([[makeQuery(id+"F0.imprint","INTERSECT",VERTEX,{"disambiguationData":[OD(0.0)],"derivedFrom":[subQ1,subQ0]}),1.0]])],"derivedFrom":subQ1});var subQ3=makeQuery(id+"F1.opExtrude","CAP_EDGE",EDGE,{"disambiguationData":[OSD([subQ1]),TDD([subQ2])],"isStart":true});var subQ4=sQuery(id+"F0.wireOp",EDGE,"E4");var subQ5=sQuery(id+"F0.wireOp",EDGE,"E3");var subQ6=sQuery(id+"F0.wireOp",EDGE,"E2");var subQ7=sQuery(id+"F0.wireOp",EDGE,"E1");var subQ8=sQuery(id+"F0.wireOp",EDGE,"E0");Q25=makeQuery(id+"F3.opShell","OFFSET_EDGE",EDGE,{"disambiguationData":[OSD([subQ8,subQ7,subQ6,subQ5,subQ4,subQ1,subQ0]),TDD([makeQuery(id+"F2.opFillet","BLEND_EDGE",EDGE,{"blendedFrom":[subQ3,makeQuery(id+"F1.opExtrude","CAP_FACE",FACE,{"disambiguationData":[OSD([subQ8,subQ7,subQ6,subQ5,subQ4,subQ1,subQ0])],"isStart":true})],"blendedInto":[makeQuery(id+"F1.opExtrude","CAP_FACE",FACE,{"disambiguationData":[OSD([subQ8,subQ7,subQ6,subQ5,subQ4,subQ1,subQ0])],"isStart":true})]}),makeQuery(id+"F2.opFillet","BLEND_EDGE",EDGE,{"blendedFrom":[subQ3,makeQuery(id+"F1.opExtrude","SWEPT_FACE",FACE,{"disambiguationData":[OSD([subQ1]),TDD([subQ2])]})],"blendedInto":[makeQuery(id+"F1.opExtrude","SWEPT_FACE",FACE,{"disambiguationData":[OSD([subQ1]),TDD([subQ2])]})]})]),OD(0.0)]});}
            var Q26;
            {var subQ0=sQuery(id+"F0.wireOp",EDGE,"E1");Q26=makeQuery(id+"F3.opShell","OFFSET_EDGE",EDGE,{"disambiguationData":[OSD([subQ0]),TDD([makeQuery(id+"F1.opExtrude","CAP_EDGE",EDGE,{"disambiguationData":[OSD([subQ0])],"isStart":true})]),OD(1.0)]});}
            var Q27;
            {var subQ0=sQuery(id+"F0.wireOp",EDGE,"E0");Q27=makeQuery(id+"F3.opShell","OFFSET_EDGE",EDGE,{"disambiguationData":[OSD([subQ0]),TDD([makeQuery(id+"F1.opExtrude","CAP_EDGE",EDGE,{"disambiguationData":[OSD([subQ0])],"isStart":true})]),OD(1.0)]});}
            var Q28;
            {var subQ0=sQuery(id+"F0.wireOp",EDGE,"E6");var subQ1=sQuery(id+"F0.wireOp",EDGE,"E5");var subQ2=makeQuery(id+"F0.imprint","IMPRINT",EDGE,{"disambiguationData":[TD([[makeQuery(id+"F0.imprint","INTERSECT",VERTEX,{"disambiguationData":[OD(2.0)],"derivedFrom":[subQ1,subQ0]}),-1.0]])],"derivedFrom":subQ0});var subQ3=makeQuery(id+"F1.opExtrude","CAP_EDGE",EDGE,{"disambiguationData":[OSD([subQ0]),TDD([subQ2])],"isStart":true});var subQ4=sQuery(id+"F0.wireOp",EDGE,"E4");var subQ5=sQuery(id+"F0.wireOp",EDGE,"E3");var subQ6=sQuery(id+"F0.wireOp",EDGE,"E2");var subQ7=sQuery(id+"F0.wireOp",EDGE,"E1");var subQ8=sQuery(id+"F0.wireOp",EDGE,"E0");Q28=makeQuery(id+"F3.opShell","OFFSET_EDGE",EDGE,{"disambiguationData":[OSD([subQ8,subQ7,subQ6,subQ5,subQ4,subQ1,subQ0]),TDD([makeQuery(id+"F2.opFillet","BLEND_EDGE",EDGE,{"blendedFrom":[subQ3,makeQuery(id+"F1.opExtrude","CAP_FACE",FACE,{"disambiguationData":[OSD([subQ8,subQ7,subQ6,subQ5,subQ4,subQ1,subQ0])],"isStart":true})],"blendedInto":[makeQuery(id+"F1.opExtrude","CAP_FACE",FACE,{"disambiguationData":[OSD([subQ8,subQ7,subQ6,subQ5,subQ4,subQ1,subQ0])],"isStart":true})]}),makeQuery(id+"F2.opFillet","BLEND_EDGE",EDGE,{"blendedFrom":[subQ3,makeQuery(id+"F1.opExtrude","SWEPT_FACE",FACE,{"disambiguationData":[OSD([subQ0]),TDD([subQ2])]})],"blendedInto":[makeQuery(id+"F1.opExtrude","SWEPT_FACE",FACE,{"disambiguationData":[OSD([subQ0]),TDD([subQ2])]})]})]),OD(1.0)]});}
            var Q29;
            {var subQ0=sQuery(id+"F0.wireOp",EDGE,"E4");Q29=makeQuery(id+"F3.opShell","OFFSET_EDGE",EDGE,{"disambiguationData":[OSD([subQ0]),TDD([makeQuery(id+"F1.opExtrude","CAP_EDGE",EDGE,{"disambiguationData":[OSD([subQ0])],"isStart":true})]),OD(2.0)]});}
            var Q30;
            {var subQ0=sQuery(id+"F0.wireOp",EDGE,"E3");Q30=makeQuery(id+"F3.opShell","OFFSET_EDGE",EDGE,{"disambiguationData":[OSD([subQ0]),TDD([makeQuery(id+"F1.opExtrude","CAP_EDGE",EDGE,{"disambiguationData":[OSD([subQ0])],"isStart":true})]),OD(1.0)]});}
            var Q31;
            {var subQ0=sQuery(id+"F0.wireOp",EDGE,"E0");Q31=makeQuery(id+"F3.opShell","OFFSET_EDGE",EDGE,{"disambiguationData":[OSD([subQ0]),TDD([makeQuery(id+"F1.opExtrude","CAP_EDGE",EDGE,{"disambiguationData":[OSD([subQ0])],"isStart":true})]),OD(2.0)]});}
            var Q32;
            {var subQ0=sQuery(id+"F0.wireOp",EDGE,"E6");var subQ1=sQuery(id+"F0.wireOp",EDGE,"E5");var subQ2=makeQuery(id+"F0.imprint","IMPRINT",EDGE,{"disambiguationData":[TD([[makeQuery(id+"F0.imprint","INTERSECT",VERTEX,{"disambiguationData":[OD(0.0)],"derivedFrom":[subQ1,subQ0]}),-1.0]])],"derivedFrom":subQ0});var subQ3=makeQuery(id+"F1.opExtrude","CAP_EDGE",EDGE,{"disambiguationData":[OSD([subQ0]),TDD([subQ2])],"isStart":true});var subQ4=sQuery(id+"F0.wireOp",EDGE,"E4");var subQ5=sQuery(id+"F0.wireOp",EDGE,"E3");var subQ6=sQuery(id+"F0.wireOp",EDGE,"E2");var subQ7=sQuery(id+"F0.wireOp",EDGE,"E1");var subQ8=sQuery(id+"F0.wireOp",EDGE,"E0");Q32=makeQuery(id+"F3.opShell","OFFSET_EDGE",EDGE,{"disambiguationData":[OSD([subQ8,subQ7,subQ6,subQ5,subQ4,subQ1,subQ0]),TDD([makeQuery(id+"F2.opFillet","BLEND_EDGE",EDGE,{"blendedFrom":[subQ3,makeQuery(id+"F1.opExtrude","CAP_FACE",FACE,{"disambiguationData":[OSD([subQ8,subQ7,subQ6,subQ5,subQ4,subQ1,subQ0])],"isStart":true})],"blendedInto":[makeQuery(id+"F1.opExtrude","CAP_FACE",FACE,{"disambiguationData":[OSD([subQ8,subQ7,subQ6,subQ5,subQ4,subQ1,subQ0])],"isStart":true})]}),makeQuery(id+"F2.opFillet","BLEND_EDGE",EDGE,{"blendedFrom":[subQ3,makeQuery(id+"F1.opExtrude","SWEPT_FACE",FACE,{"disambiguationData":[OSD([subQ0]),TDD([subQ2])]})],"blendedInto":[makeQuery(id+"F1.opExtrude","SWEPT_FACE",FACE,{"disambiguationData":[OSD([subQ0]),TDD([subQ2])]})]})]),OD(0.0)]});}
            var Q33;
            {var subQ0=sQuery(id+"F0.wireOp",EDGE,"E2");Q33=makeQuery(id+"F3.opShell","OFFSET_EDGE",EDGE,{"disambiguationData":[OSD([subQ0]),TDD([makeQuery(id+"F1.opExtrude","CAP_EDGE",EDGE,{"disambiguationData":[OSD([subQ0])],"isStart":true})]),OD(2.0)]});}
            var Q34;
            {var subQ0=sQuery(id+"F0.wireOp",EDGE,"E4");Q34=makeQuery(id+"F3.opShell","OFFSET_EDGE",EDGE,{"disambiguationData":[OSD([subQ0]),TDD([makeQuery(id+"F1.opExtrude","CAP_EDGE",EDGE,{"disambiguationData":[OSD([subQ0])],"isStart":true})]),OD(1.0)]});}
            var Q35;
            {var subQ0=sQuery(id+"F0.wireOp",EDGE,"E0");Q35=makeQuery(id+"F3.opShell","OFFSET_EDGE",EDGE,{"disambiguationData":[OSD([subQ0]),TDD([makeQuery(id+"F1.opExtrude","CAP_EDGE",EDGE,{"disambiguationData":[OSD([subQ0])],"isStart":true})]),OD(3.0)]});}
            var Q36;
            {var subQ0=sQuery(id+"F0.wireOp",EDGE,"E2");Q36=makeQuery(id+"F3.opShell","OFFSET_EDGE",EDGE,{"disambiguationData":[OSD([subQ0]),TDD([makeQuery(id+"F1.opExtrude","CAP_EDGE",EDGE,{"disambiguationData":[OSD([subQ0])],"isStart":true})]),OD(1.0)]});}
            var Q37;
            {var subQ0=sQuery(id+"F0.wireOp",EDGE,"E6");var subQ1=sQuery(id+"F0.wireOp",EDGE,"E5");var subQ2=makeQuery(id+"F0.imprint","IMPRINT",EDGE,{"disambiguationData":[TD([[makeQuery(id+"F0.imprint","INTERSECT",VERTEX,{"disambiguationData":[OD(2.0)],"derivedFrom":[subQ1,subQ0]}),-1.0]])],"derivedFrom":subQ0});var subQ3=makeQuery(id+"F1.opExtrude","CAP_EDGE",EDGE,{"disambiguationData":[OSD([subQ0]),TDD([subQ2])],"isStart":true});var subQ4=sQuery(id+"F0.wireOp",EDGE,"E4");var subQ5=sQuery(id+"F0.wireOp",EDGE,"E3");var subQ6=sQuery(id+"F0.wireOp",EDGE,"E2");var subQ7=sQuery(id+"F0.wireOp",EDGE,"E1");var subQ8=sQuery(id+"F0.wireOp",EDGE,"E0");Q37=makeQuery(id+"F3.opShell","OFFSET_EDGE",EDGE,{"disambiguationData":[OSD([subQ8,subQ7,subQ6,subQ5,subQ4,subQ1,subQ0]),TDD([makeQuery(id+"F2.opFillet","BLEND_EDGE",EDGE,{"blendedFrom":[subQ3,makeQuery(id+"F1.opExtrude","CAP_FACE",FACE,{"disambiguationData":[OSD([subQ8,subQ7,subQ6,subQ5,subQ4,subQ1,subQ0])],"isStart":true})],"blendedInto":[makeQuery(id+"F1.opExtrude","CAP_FACE",FACE,{"disambiguationData":[OSD([subQ8,subQ7,subQ6,subQ5,subQ4,subQ1,subQ0])],"isStart":true})]}),makeQuery(id+"F2.opFillet","BLEND_EDGE",EDGE,{"blendedFrom":[subQ3,makeQuery(id+"F1.opExtrude","SWEPT_FACE",FACE,{"disambiguationData":[OSD([subQ0]),TDD([subQ2])]})],"blendedInto":[makeQuery(id+"F1.opExtrude","SWEPT_FACE",FACE,{"disambiguationData":[OSD([subQ0]),TDD([subQ2])]})]})]),OD(0.0)]});}
            var Q38;
            {var subQ0=sQuery(id+"F0.wireOp",EDGE,"E6");var subQ1=sQuery(id+"F0.wireOp",EDGE,"E5");var subQ2=makeQuery(id+"F0.imprint","IMPRINT",EDGE,{"disambiguationData":[TD([[makeQuery(id+"F0.imprint","INTERSECT",VERTEX,{"disambiguationData":[OD(1.0)],"derivedFrom":[subQ1,subQ0]}),-1.0]])],"derivedFrom":subQ1});var subQ3=makeQuery(id+"F1.opExtrude","CAP_EDGE",EDGE,{"disambiguationData":[OSD([subQ1]),TDD([subQ2])],"isStart":true});var subQ4=sQuery(id+"F0.wireOp",EDGE,"E4");var subQ5=sQuery(id+"F0.wireOp",EDGE,"E3");var subQ6=sQuery(id+"F0.wireOp",EDGE,"E2");var subQ7=sQuery(id+"F0.wireOp",EDGE,"E1");var subQ8=sQuery(id+"F0.wireOp",EDGE,"E0");Q38=makeQuery(id+"F3.opShell","OFFSET_EDGE",EDGE,{"disambiguationData":[OSD([subQ8,subQ7,subQ6,subQ5,subQ4,subQ1,subQ0]),TDD([makeQuery(id+"F2.opFillet","BLEND_EDGE",EDGE,{"blendedFrom":[subQ3,makeQuery(id+"F1.opExtrude","CAP_FACE",FACE,{"disambiguationData":[OSD([subQ8,subQ7,subQ6,subQ5,subQ4,subQ1,subQ0])],"isStart":true})],"blendedInto":[makeQuery(id+"F1.opExtrude","CAP_FACE",FACE,{"disambiguationData":[OSD([subQ8,subQ7,subQ6,subQ5,subQ4,subQ1,subQ0])],"isStart":true})]}),makeQuery(id+"F2.opFillet","BLEND_EDGE",EDGE,{"blendedFrom":[subQ3,makeQuery(id+"F1.opExtrude","SWEPT_FACE",FACE,{"disambiguationData":[OSD([subQ1]),TDD([subQ2])]})],"blendedInto":[makeQuery(id+"F1.opExtrude","SWEPT_FACE",FACE,{"disambiguationData":[OSD([subQ1]),TDD([subQ2])]})]})]),OD(0.0)]});}
            var Q39;
            {var subQ0=sQuery(id+"F0.wireOp",EDGE,"E6");var subQ1=sQuery(id+"F0.wireOp",EDGE,"E5");var subQ2=makeQuery(id+"F0.imprint","IMPRINT",EDGE,{"disambiguationData":[TD([[makeQuery(id+"F0.imprint","INTERSECT",VERTEX,{"disambiguationData":[OD(1.0)],"derivedFrom":[subQ1,subQ0]}),-1.0]])],"derivedFrom":subQ1});var subQ3=makeQuery(id+"F1.opExtrude","CAP_EDGE",EDGE,{"disambiguationData":[OSD([subQ1]),TDD([subQ2])],"isStart":true});var subQ4=sQuery(id+"F0.wireOp",EDGE,"E4");var subQ5=sQuery(id+"F0.wireOp",EDGE,"E3");var subQ6=sQuery(id+"F0.wireOp",EDGE,"E2");var subQ7=sQuery(id+"F0.wireOp",EDGE,"E1");var subQ8=sQuery(id+"F0.wireOp",EDGE,"E0");Q39=makeQuery(id+"F3.opShell","OFFSET_EDGE",EDGE,{"disambiguationData":[OSD([subQ8,subQ7,subQ6,subQ5,subQ4,subQ1,subQ0]),TDD([makeQuery(id+"F2.opFillet","BLEND_EDGE",EDGE,{"blendedFrom":[subQ3,makeQuery(id+"F1.opExtrude","CAP_FACE",FACE,{"disambiguationData":[OSD([subQ8,subQ7,subQ6,subQ5,subQ4,subQ1,subQ0])],"isStart":true})],"blendedInto":[makeQuery(id+"F1.opExtrude","CAP_FACE",FACE,{"disambiguationData":[OSD([subQ8,subQ7,subQ6,subQ5,subQ4,subQ1,subQ0])],"isStart":true})]}),makeQuery(id+"F2.opFillet","BLEND_EDGE",EDGE,{"blendedFrom":[subQ3,makeQuery(id+"F1.opExtrude","SWEPT_FACE",FACE,{"disambiguationData":[OSD([subQ1]),TDD([subQ2])]})],"blendedInto":[makeQuery(id+"F1.opExtrude","SWEPT_FACE",FACE,{"disambiguationData":[OSD([subQ1]),TDD([subQ2])]})]})]),OD(1.0)]});}
            fillet(context, id + "F4", {"entities" : qUnion([Q0, Q1, Q2, Q3, Q4, Q5, Q6, Q7, Q8, Q9, Q10, Q11, Q12, Q13, Q14, Q15, Q16, Q17, Q18, Q19, Q20, Q21, Q22, Q23, Q24, Q25, Q26, Q27, Q28, Q29, Q30, Q31, Q32, Q33, Q34, Q35, Q36, Q37, Q38, Q39]), "radius" : 0.5 * mm, "tangentPropagation" : true, "allowEdgeOverflow" : false});
        }
    });
